# Revit family: EL-AQ0622xxWS840M9P0600
name_source: partatom
category: Leuchten
units: mm (PartAtom-declared; Revit-internal decimal feet)

## family parameters
Basisbauteil = Fläche
Beim Laden mit Abzugskörper schneiden = Nein
Bemaßung runder Anschluss = Durchmesser verwenden
Gemeinsam genutzt = Nein
Lichtquelle = Ja
OmniClass-Nummer = 23.80.70.11
OmniClass-Titel = Luminaries for Internal Lighting
Raumberechnungspunkt = Nein
Teiletyp = Normal

## types (2) — shared parameters
Baugruppenkennzeichen = D5020200
Datei für fotometrisches Netz = xxxM9Pxxx.IES
Emissionsform beim Rendern sichtbar = Nein
Farbfilter = 16777215
Farbtemperaturverschiebung bei Dämpfen der Lampe = <Keine Auswahl>
Hersteller = RIDI Leuchten GmbH
Lampe = LED
Neigungswinkel = 90.00°
Scheinlast = 37 VA
URL = www.ridi.de
Von Breite des Rechtecks ausssenden = 540 mm  [stored 1.77165 ft]
Von Länge des Rechtecks aussenden = 514 mm  [stored 1.68635 ft]
brand = RIDI
conformity mark = CE
electrical safety class = 1
height = 60 mm  [stored 0.19685 ft]
ingress protection (IP) code = IP20
length = 630 mm  [stored 2.06693 ft]
nominal frequency = 50-60Hz
nominal voltage = 230
rated input power = 37
voltage type (AC, DC, UC) = AC
width = 626 mm  [stored 2.05381 ft]
zero-valued in all types: Vorgabe-Ansicht

## per-type parameters (varying)
| type | Modell | product name |
| EL-AQ0622RFWS840M9P0600 | 0627909 | EL-AQ0622RFWS840M9P0600

 EL-AQ0622RFWS840M9P0600
 EL-AQ0622RFWS840M9P0600 |
| EL-AQ0622DAWS840M9P0600 | 0637909 | EL-AQ0622DAWS840M9P0600
EL-AQ0622DAWS840M9P0600
EL-AQ0622DAWS840M9P0600
EL-AQ0622DAWS840M9P0600
 EL-AQ0622RFWS840M9P0600 |

note: [stored X ft] marks values corroborated as IEEE doubles in the binary element streams (Revit-internal decimal feet)
